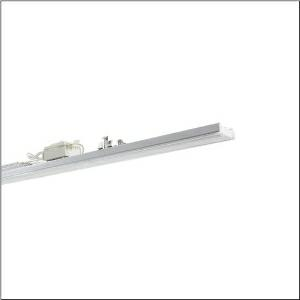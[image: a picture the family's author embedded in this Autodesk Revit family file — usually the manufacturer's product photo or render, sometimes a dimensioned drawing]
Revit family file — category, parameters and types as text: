
# Revit family: licross_r__11_recessed_mo_51tl18de445g_0991
name_source: partatom
category: Lighting Fixtures
units: mm (PartAtom-declared; Revit-internal decimal feet)

## family parameters
Cut with Voids When Loaded = No
Host = Face
Light Source = No
Part Type = Normal
Room Calculation Point = No
Round Connector Dimension = Use Diameter
Shared = No

## types (1)
- --- (1 x LED, 4970 lm, 29.6 W, 4000K)
    Apparent Load = 30 VA
    CIE Flux Codes = 83 96 99 100 100
    Color Rendering = 80
    Color Temperature = 4000K
    Default Elevation = 1800 mm
    Description = Licross® 11 Recessed MO, luminaire insert, of sheet steel, coil coated, white, length: 750mm, width: 66mm, height: 67mm, LED rated luminous flux: 4.970lm, light colour: 840, control gear: DALI 2, with plug, 5-pole, with phase selection, mains connection: 220..240V, AC, 50/60Hz, rated input power: 30W, halogen-free wiring, primary light control with lens, of plastic, primary optical cover: cover, of PMMA, light emission: direct distribution, primary light characteristic: symmetric, protection rating (complete): IP40, insulation class (complete): insulation class I (protective earthing), certification: CE, ENEC, VDE, UKCA, protection symbol: D if used in an environment without relevant dust loads with corresponding accessories, impact resistance: IK06, permissible ambient temperature for indoor applications: -25..+35°C, corresponds to IFS (International Featured Standards) requirements for safety and quality in the food industry, reducing of maximum allowable ambient temperature of 5°C with ceiling mounting, LABS conformity tested according to VDMA 24364:2018-05, packaging unit: 1 piece
    Height = 58 mm
    Lamp = 1 x LED
    Lamp Light Flux = 4970 lm
    Lamp Power = 29.6 W
    Lamp count = 1
    Length = 750 mm
    Luminous efficacy = 168 lm/W
    Manufacturer = Siteco
    ModVariant = No
    Model = 51TL18DE445G
    Mounting Place = Ceiling
    Mounting Type = Pendant
    Number of Poles = 1
    OnlyDefault = Yes
    Power Factor = 1
    Product Name = Licross® 11 Recessed MO
    Product group = luminaire insert
    ProductGroupID = 902
    Protection Class = Protection class I
    Protection Degree = IP 40
    RLX_Detail_Level = 1
    RLX_Emergency_Light_Flux = 0 lm
    RLX_Emergency_Type = 0
    RLX_Emergency_Type_DB = No
    RlxData = <blob elided: 29173 chars, md5=c57c2a28>
    Socket = socket
    Standby Power = 0 W
    System Light Flux = 4970 lm
    System Power = 30 W
    Type Comments = factory setting: luminous flux: 100 % | dim-lin: 254 | 378 mA
    Type Image = l_1296930.jpg
    URL = http://relux.com
    VarID = @adj_098990
    Voltage = 0 V
    Weight = 0.00 kg
    Width = 66 mm

## geometry (parser evidence)
native form markers: Blend x4, Sweep x10
no freeform markers — native parametric forms only
